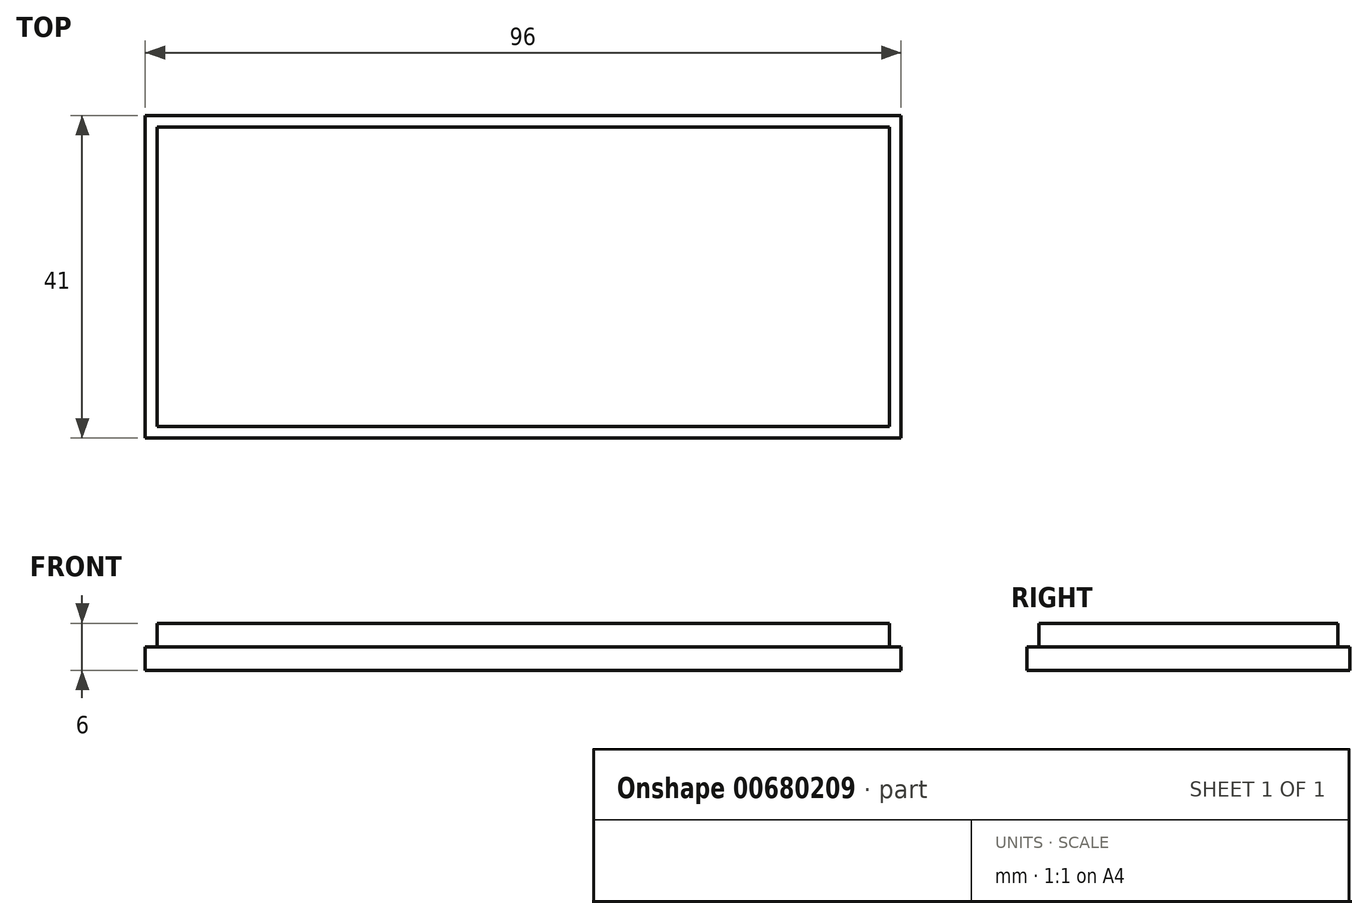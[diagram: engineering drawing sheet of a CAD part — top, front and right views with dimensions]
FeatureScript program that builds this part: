
annotation { "Feature Type Name" : "Feature", "Feature Type Description" : "" }
export const myFeature = defineFeature(function(context is Context, id is Id, definition is map)
    precondition{}
    {
        {
            var Q0;
            Q0=qCreatedBy(makeId("Top.planeOp"),FACE);
            var sketch = newSketch(context, id + "F0", { "sketchPlane" : qUnion([Q0])});
            skLineSegment(sketch, "E0.bottom", {"start": v(-53.82, 21) * mm, "end": v(42.18, 21) * mm});
            skLineSegment(sketch, "E0.top", {"start": v(-53.82, -20) * mm, "end": v(42.18, -20) * mm});
            skLineSegment(sketch, "E0.left", {"start": v(-53.82, 21) * mm, "end": v(-53.82, -20) * mm});
            skLineSegment(sketch, "E0.right", {"start": v(42.18, 21) * mm, "end": v(42.18, -20) * mm});
            skSolve(sketch);
        }
        {
            var Q0;
            Q0=qSketchRegion(id+"F0",true);
            extrude(context, id + "F1", {"entities" : qUnion([Q0]), "depth" : 3 * mm, "offsetDistance" : 25 * mm});
        }
        {
            var Q0;
            Q0=makeQuery(id+"F1.opExtrude","CAP_FACE",FACE,{"disambiguationData":[OSD([sQuery(id+"F0.wireOp",EDGE,"E0.bottom"),sQuery(id+"F0.wireOp",EDGE,"E0.top"),sQuery(id+"F0.wireOp",EDGE,"E0.left"),sQuery(id+"F0.wireOp",EDGE,"E0.right")])],"isStart":false});
            var sketch = newSketch(context, id + "F2", { "sketchPlane" : qUnion([Q0])});
            skLineSegment(sketch, "E1.bottom", {"start": v(-52.32, 19.5) * mm, "end": v(40.68, 19.5) * mm});
            skLineSegment(sketch, "E1.top", {"start": v(-52.32, -18.5) * mm, "end": v(40.68, -18.5) * mm});
            skLineSegment(sketch, "E1.left", {"start": v(-52.32, 19.5) * mm, "end": v(-52.32, -18.5) * mm});
            skLineSegment(sketch, "E1.right", {"start": v(40.68, 19.5) * mm, "end": v(40.68, -18.5) * mm});
            skSolve(sketch);
        }
        {
            var Q0;
            Q0=makeQuery(id+"F2.imprint","IMPRINT",FACE,{"disambiguationData":[TD([[makeQuery(id+"F2.imprint","IMPRINT",EDGE,{"derivedFrom":sQuery(id+"F2.wireOp",EDGE,"E1.bottom")}),-1.0]])]});
            extrude(context, id + "F3", {"entities" : qUnion([Q0]), "operationType" : NewBodyOperationType.ADD, "depth" : 3 * mm, "offsetDistance" : 25 * mm});
        }
    });
